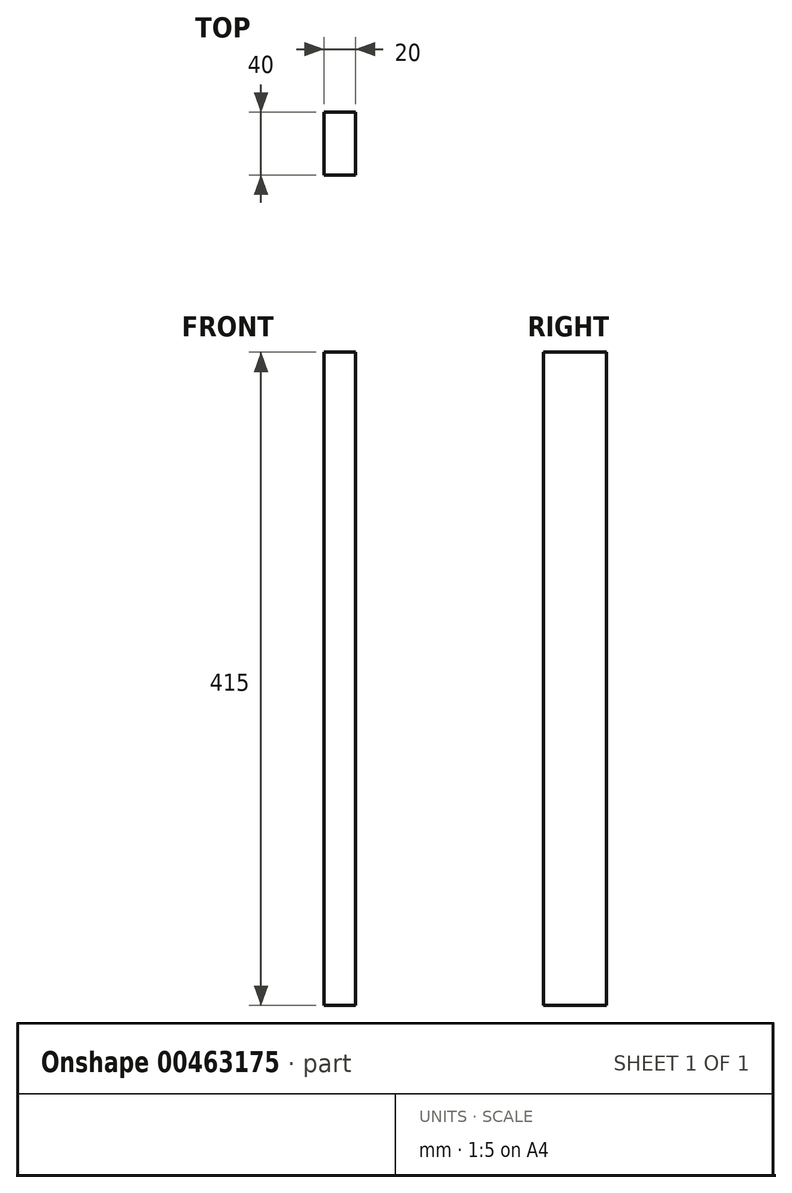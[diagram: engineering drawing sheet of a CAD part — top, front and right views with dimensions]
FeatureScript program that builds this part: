
annotation { "Feature Type Name" : "Feature", "Feature Type Description" : "" }
export const myFeature = defineFeature(function(context is Context, id is Id, definition is map)
    precondition{}
    {
        {
            var Q0;
            Q0=qCreatedBy(makeId("Top.planeOp"),FACE);
            var sketch = newSketch(context, id + "F0", { "sketchPlane" : qUnion([Q0])});
            skLineSegment(sketch, "E0.bottom", {"start": v(0, 0) * mm, "end": v(20, 0) * mm});
            skLineSegment(sketch, "E0.top", {"start": v(0, -40) * mm, "end": v(20, -40) * mm});
            skLineSegment(sketch, "E0.left", {"start": v(0, 0) * mm, "end": v(0, -40) * mm});
            skLineSegment(sketch, "E0.right", {"start": v(20, 0) * mm, "end": v(20, -40) * mm});
            skSolve(sketch);
        }
        {
            var Q0;
            Q0 = qSketchRegion(id + "F0", true);
            extrude(context, id + "F1", {"entities" : qUnion([Q0]), "depth" : 400 * mm});
        }
        {
            var Q0;
            Q0=makeQuery(id+"F0.imprint","IMPRINT",FACE,{"disambiguationData":[TD([[makeQuery(id+"F0.imprint","IMPRINT",EDGE,{"derivedFrom":sQuery(id+"F0.wireOp",EDGE,"E0.bottom")}),-1.0]])]});
            extrude(context, id + "F2", {"entities" : qUnion([Q0]), "operationType" : NewBodyOperationType.ADD, "oppositeDirection" : true, "depth" : 15 * mm});
        }
    });
